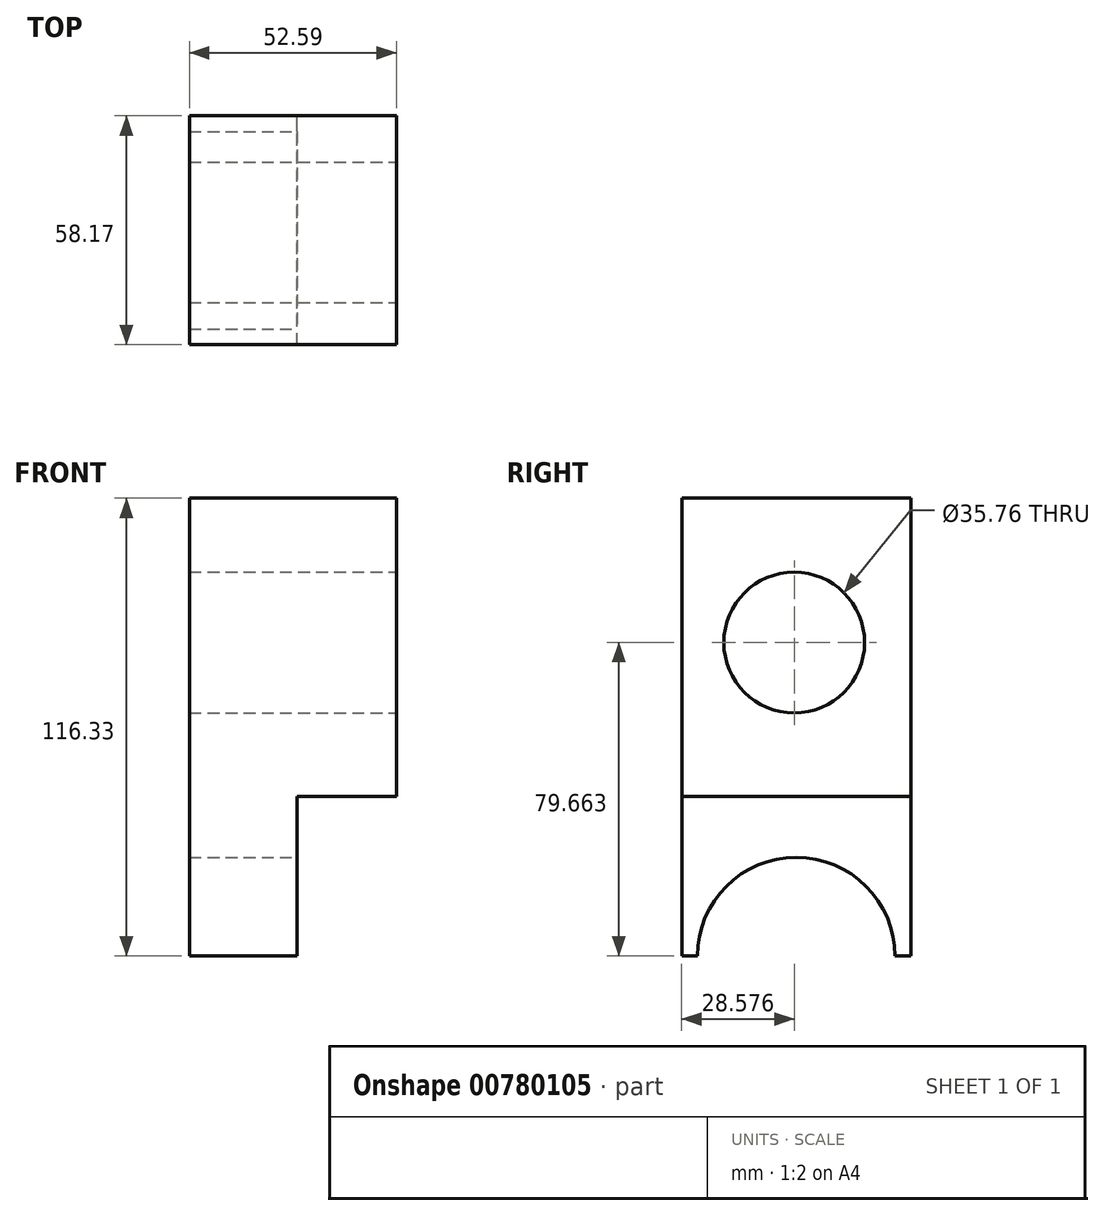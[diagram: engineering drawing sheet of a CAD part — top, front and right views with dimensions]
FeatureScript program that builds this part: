
annotation { "Feature Type Name" : "Feature", "Feature Type Description" : "" }
export const myFeature = defineFeature(function(context is Context, id is Id, definition is map)
    precondition{}
    {
        {
            var Q0;
            Q0=qCreatedBy(makeId("Front.planeOp"),FACE);
            var sketch = newSketch(context, id + "F0", { "sketchPlane" : qUnion([Q0])});
            skLineSegment(sketch, "E0", {"start": v(0, 0) * mm, "end": v(25.19, 0) * mm});
            skLineSegment(sketch, "E1", {"start": v(25.19, 0) * mm, "end": v(25.19, 75.83) * mm});
            skLineSegment(sketch, "E2", {"start": v(25.19, 75.83) * mm, "end": v(-27.4, 75.83) * mm});
            skLineSegment(sketch, "E3", {"start": v(-27.4, 75.83) * mm, "end": v(-27.4, -40.5) * mm});
            skLineSegment(sketch, "E4", {"start": v(-27.4, -40.5) * mm, "end": v(0, -40.5) * mm});
            skLineSegment(sketch, "E5", {"start": v(0, -40.5) * mm, "end": v(0, 0) * mm});
            skSolve(sketch);
        }
        {
            var Q0;
            Q0=makeQuery(id+"F0.imprint","IMPRINT",FACE,{"disambiguationData":[TD([[makeQuery(id+"F0.imprint","IMPRINT",EDGE,{"derivedFrom":sQuery(id+"F0.wireOp",EDGE,"E0")}),1.0]])]});
            extrude(context, id + "F1", {"entities" : qUnion([Q0]), "depth" : 58.17 * mm, "offsetDistance" : 25.4 * mm});
        }
        {
            var Q0;
            Q0=makeQuery(id+"F1.opExtrude","SWEPT_FACE",FACE,{"disambiguationData":[OSD([sQuery(id+"F0.wireOp",EDGE,"E1")])]});
            var sketch = newSketch(context, id + "F2", { "sketchPlane" : qUnion([Q0])});
            skCircle(sketch, "E6", {"center": v(-29.6, 39.16) * mm, "radius": 17.88 * mm});
            skSolve(sketch);
        }
        {
            var Q0;
            Q0=makeQuery(id+"F2.imprint","IMPRINT",FACE,{"disambiguationData":[TD([[makeQuery(id+"F2.imprint","IMPRINT",EDGE,{"derivedFrom":sQuery(id+"F2.wireOp",EDGE,"E6")}),1.0]])]});
            extrude(context, id + "F3", {"entities" : qUnion([Q0]), "operationType" : NewBodyOperationType.REMOVE, "endBound" : BoundingType.THROUGH_ALL, "oppositeDirection" : true, "depth" : 25.4 * mm, "offsetDistance" : 25.4 * mm});
        }
        {
            var Q0;
            Q0=makeQuery(id+"F1.opExtrude","SWEPT_FACE",FACE,{"disambiguationData":[OSD([sQuery(id+"F0.wireOp",EDGE,"E5")])]});
            var sketch = newSketch(context, id + "F4", { "sketchPlane" : qUnion([Q0])});
            skCircle(sketch, "E7", {"center": v(-29.08, -40.5) * mm, "radius": 25.1 * mm});
            skSolve(sketch);
        }
        {
            var Q0;
            {var subQ0=sQuery(id+"F4.wireOp",EDGE,"E7");var subQ1=makeQuery(id+"F1.opExtrude","SWEPT_EDGE",EDGE,{"disambiguationData":[OSD([sQuery(id+"F0.wireOp",EDGE,"E4"),sQuery(id+"F0.wireOp",EDGE,"E5")])]});var subQ2=makeQuery(id+"F4.imprint","INTERSECT",VERTEX,{"disambiguationData":[OD(0.0)],"derivedFrom":[subQ1,subQ0]});Q0=makeQuery(id+"F4.imprint","IMPRINT",FACE,{"disambiguationData":[TD([[makeQuery(id+"F4.imprint","IMPRINT",EDGE,{"disambiguationData":[TD([[subQ2,-1.0]])],"derivedFrom":subQ0}),1.0]])]});}
            extrude(context, id + "F5", {"entities" : qUnion([Q0]), "operationType" : NewBodyOperationType.REMOVE, "endBound" : BoundingType.THROUGH_ALL, "oppositeDirection" : true, "depth" : 25.4 * mm, "offsetDistance" : 25.4 * mm});
        }
    });
